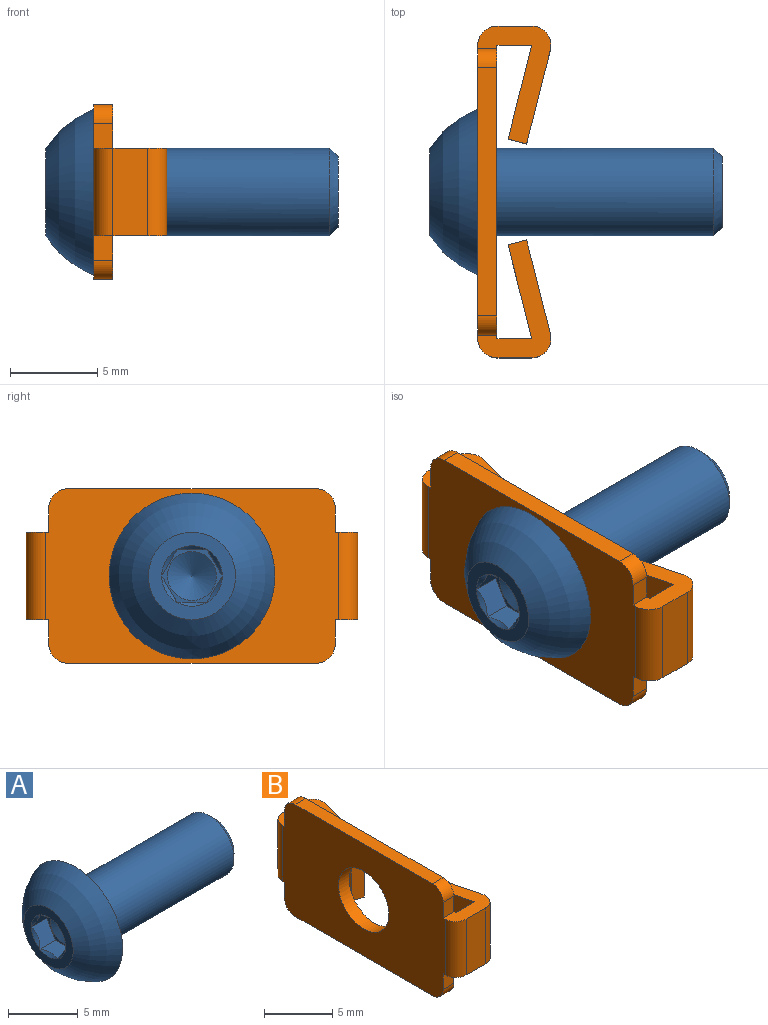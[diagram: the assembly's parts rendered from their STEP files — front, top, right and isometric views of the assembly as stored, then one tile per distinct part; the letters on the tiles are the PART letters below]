
ASSEMBLY  parts=2 mates=1
PART A: 21 faces, bbox 16.8x9.5x9.5 mm
  f0: cone r=1.4mm half-angle=45deg, axis (-1,0,0), area 0.4mm2, adj f8,f13
  f1: cone r=1.4mm half-angle=45deg, axis (-1,0,0), area 0.4mm2, adj f8,f14
  f2: cone r=1.4mm half-angle=45deg, axis (-1,0,0), area 0.4mm2, adj f8,f15
  f3: cone r=1.4mm half-angle=45deg, axis (-1,0,0), area 0.4mm2, adj f8,f16
  f4: cone r=1.4mm half-angle=45deg, axis (-1,0,0), area 0.4mm2, adj f8,f17
  f5: cone r=1.4mm half-angle=45deg, axis (-1,0,0), area 0.4mm2, adj f8,f18
  f6: plane 9.5x9.5mm, normal (1,0,0), area 43.5mm2, adj f7,f9
  f7: revolved ~9.5x9.5mm, area 85.6mm2, adj f6,f8
  f8: plane 5x5mm, normal (-1,0,0), area 10.2mm2, adj f0,f1,f2,f3,f4,f5,f7
  f9: torus R=2.95mm, axis (1,0,0), area 11.8mm2, adj f6,f12
  f10: plane 4.02x4.02mm, normal (1,0,0), area 12.7mm2, adj f11
  f11: cone r=2.01mm half-angle=45deg, axis (-1,0,0), area 9.8mm2, adj f10,f12
  f12: cylinder r=2.5mm len=13.06mm, axis (-1,0,0), area 205.1mm2, adj f9,f11
  f13: plane 1.73x1.56mm, normal (0,0,-1), area 2.4mm2, adj f0,f14,f18,f19
  f14: plane 1.56x1.5mm, normal (0,0.87,-0.5), area 2.4mm2, adj f1,f13,f15,f19
  f15: plane 1.56x1.5mm, normal (0,0.87,0.5), area 2.4mm2, adj f2,f14,f16,f19
  f16: plane 1.73x1.56mm, normal (0,0,1), area 2.4mm2, adj f3,f15,f17,f19
  f17: plane 1.56x1.5mm, normal (0,-0.87,0.5), area 2.4mm2, adj f4,f16,f18,f19
  f18: plane 1.56x1.5mm, normal (0,-0.87,-0.5), area 2.4mm2, adj f5,f13,f17,f19
  f19: plane 3.46x3mm, normal (-1,0,0), area 1.6mm2, adj f13,f14,f15,f16,f17,f18,f20
  f20: cone r=0mm half-angle=60deg, axis (-1,0,0), area 7.1mm2, adj f19
PART B: 31 faces, bbox 4.2x19x10 mm
  f0: plane 5x1.07mm, normal (-0.24,0.97,0), area 5.5mm2, adj f1,f3,f17,f19
  f1: plane 5.38x5mm, normal (0.97,0.24,0), area 27.7mm2, adj f0,f17,f19,f27
  f2: plane 5.38x5mm, normal (0.97,-0.24,0), area 27.7mm2, adj f5,f14,f21,f28
  f3: plane 5.38x5mm, normal (-0.97,-0.24,0), area 27.7mm2, adj f0,f11,f17,f19
  f4: plane 5.38x5mm, normal (-0.97,0.24,0), area 27.7mm2, adj f5,f12,f14,f21
  f5: plane 5x1.07mm, normal (-0.24,-0.97,0), area 5.5mm2, adj f2,f4,f14,f21
  f6: plane 5x1.99mm, normal (0,-1,0), area 9.9mm2, adj f17,f19,f27,f29
  f7: plane 5x1.99mm, normal (0,1,0), area 9.9mm2, adj f14,f21,f28,f30
  f8: plane 14.2x1.1mm, normal (0,0,-1), area 15.6mm2, adj f10,f13,f24,f26
  f9: plane 14.2x1.1mm, normal (0,0,1), area 15.6mm2, adj f10,f13,f23,f25
  f10: plane 16.8x10mm, normal (-1,0,0), area 143.7mm2, adj f8,f9,f14,f15,f16,f17,f18,f19
  f11: plane 5x1.99mm, normal (0,1,0), area 9.9mm2, adj f3,f13,f17,f19
  f12: plane 5x1.99mm, normal (0,-1,0), area 9.9mm2, adj f4,f13,f14,f21
  f13: plane 16.8x10mm, normal (1,0,0), area 143.7mm2, adj f8,f9,f11,f12,f14,f15,f16,f17
  f14: plane 6.75x4.19mm, normal (0,0,-1), area 10.6mm2, adj f2,f4,f5,f7,f10,f12,f13,f15
  f15: plane 1.4x1.1mm, normal (0,1,0), area 1.5mm2, adj f10,f13,f14,f26
  f16: cylinder r=2.6mm len=5.2mm, axis (-1,0,0), area 18mm2, adj f10,f13
  f17: plane 6.75x4.19mm, normal (0,0,1), area 10.6mm2, adj f0,f1,f3,f6,f10,f11,f13,f18
  f18: plane 1.4x1.1mm, normal (0,-1,0), area 1.5mm2, adj f10,f13,f17,f25
  f19: plane 6.75x4.19mm, normal (0,0,-1), area 10.6mm2, adj f0,f1,f3,f6,f10,f11,f13,f20
  f20: plane 1.4x1.1mm, normal (0,-1,0), area 1.5mm2, adj f10,f13,f19,f24
  f21: plane 6.75x4.19mm, normal (0,0,1), area 10.6mm2, adj f2,f4,f5,f7,f10,f12,f13,f22
  f22: plane 1.4x1.1mm, normal (0,1,0), area 1.5mm2, adj f10,f13,f21,f23
  f23: cylinder r=1.1mm len=1.1mm, axis (-1,0,0), area 1.9mm2, adj f9,f10,f13,f22
  f24: cylinder r=1.1mm len=1.1mm, axis (1,0,0), area 1.9mm2, adj f8,f10,f13,f20
  f25: cylinder r=1.1mm len=1.1mm, axis (1,0,0), area 1.9mm2, adj f9,f10,f13,f18
  f26: cylinder r=1.1mm len=1.1mm, axis (-1,0,0), area 1.9mm2, adj f8,f10,f13,f15
  f27: cylinder r=1.1mm len=5mm, axis (0,0,1), area 10mm2, adj f1,f6,f17,f19
  f28: cylinder r=1.1mm len=5mm, axis (0,0,1), area 10mm2, adj f2,f7,f14,f21
  f29: cylinder r=1.1mm len=5mm, axis (0,0,1), area 8.6mm2, adj f6,f10,f17,f19
  f30: cylinder r=1.1mm len=5mm, axis (0,0,1), area 8.6mm2, adj f7,f10,f14,f21
PLACE A t=(-5.47,0.92,-2.74)mm
PLACE B t=(-5.47,0.92,-2.74)mm
MATE fastened B.f16 <-> A.f11  axis (-1,0,0) through (-5.47,0.92,-2.74)mm
